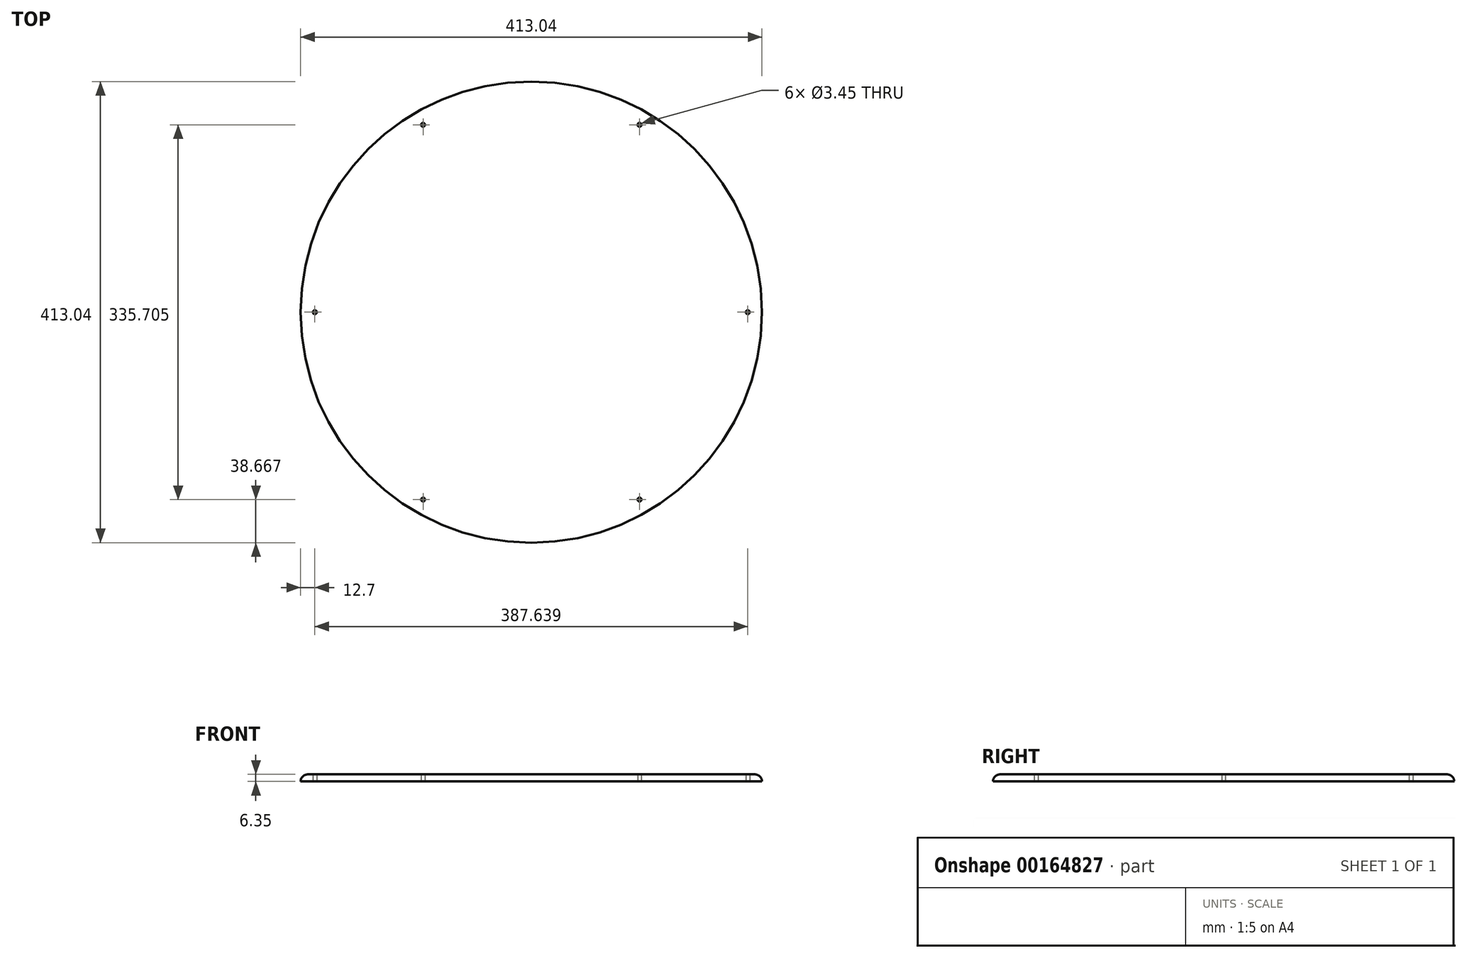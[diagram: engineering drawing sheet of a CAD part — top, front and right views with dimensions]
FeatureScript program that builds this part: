
annotation { "Feature Type Name" : "Feature", "Feature Type Description" : "" }
export const myFeature = defineFeature(function(context is Context, id is Id, definition is map)
    precondition{}
    {
        {
            var Q0;
            Q0=qCreatedBy(makeId("Top.planeOp"),FACE);
            var sketch = newSketch(context, id + "F0", { "sketchPlane" : qUnion([Q0])});
            skCircle(sketch, "E0", {"center": v(0, 0) * mm, "radius": 206.52 * mm});
            skCircle(sketch, "E1.cCircle", {"center": v(0, 0) * mm, "radius": 167.85 * mm, "construction": true});
            skLineSegment(sketch, "E1.0", {"start": v(-96.9, 167.85) * mm, "end": v(96.9, 167.85) * mm, "construction": true});
            skLineSegment(sketch, "E1.1", {"start": v(96.9, 167.85) * mm, "end": v(193.82, 0) * mm, "construction": true});
            skLineSegment(sketch, "E1.2", {"start": v(193.82, 0) * mm, "end": v(96.9, -167.85) * mm, "construction": true});
            skLineSegment(sketch, "E1.3", {"start": v(96.9, -167.85) * mm, "end": v(-96.9, -167.85) * mm, "construction": true});
            skLineSegment(sketch, "E1.4", {"start": v(-96.9, -167.85) * mm, "end": v(-193.82, 0) * mm, "construction": true});
            skLineSegment(sketch, "E1.5", {"start": v(-193.82, 0) * mm, "end": v(-96.9, 167.85) * mm, "construction": true});
            skCircle(sketch, "E2", {"center": v(96.9, 167.85) * mm, "radius": 12.7 * mm, "construction": true});
            skCircle(sketch, "E3", {"center": v(96.9, 167.85) * mm, "radius": 1.73 * mm});
            skCircle(sketch, "E4", {"center": v(193.82, 0) * mm, "radius": 1.73 * mm});
            skCircle(sketch, "E5", {"center": v(96.9, -167.85) * mm, "radius": 1.73 * mm});
            skCircle(sketch, "E6", {"center": v(-96.9, -167.85) * mm, "radius": 1.73 * mm});
            skCircle(sketch, "E7", {"center": v(-193.82, 0) * mm, "radius": 1.73 * mm});
            skCircle(sketch, "E8", {"center": v(-96.9, 167.85) * mm, "radius": 1.73 * mm});
            skSolve(sketch);
        }
        {
            var Q0;
            Q0=qSketchRegion(id+"F0",true);
            extrude(context, id + "F1", {"entities" : qUnion([Q0]), "depth" : 6.35 * mm});
        }
        {
            var Q0;
            Q0=makeQuery(id+"F1.opExtrude","CAP_EDGE",EDGE,{"disambiguationData":[OSD([sQuery(id+"F0.wireOp",EDGE,"E0")])],"isStart":false});
            fillet(context, id + "F2", {"entities" : qUnion([Q0]), "radius" : 6.35 * mm, "tangentPropagation" : true, "allowEdgeOverflow" : false});
        }
    });
